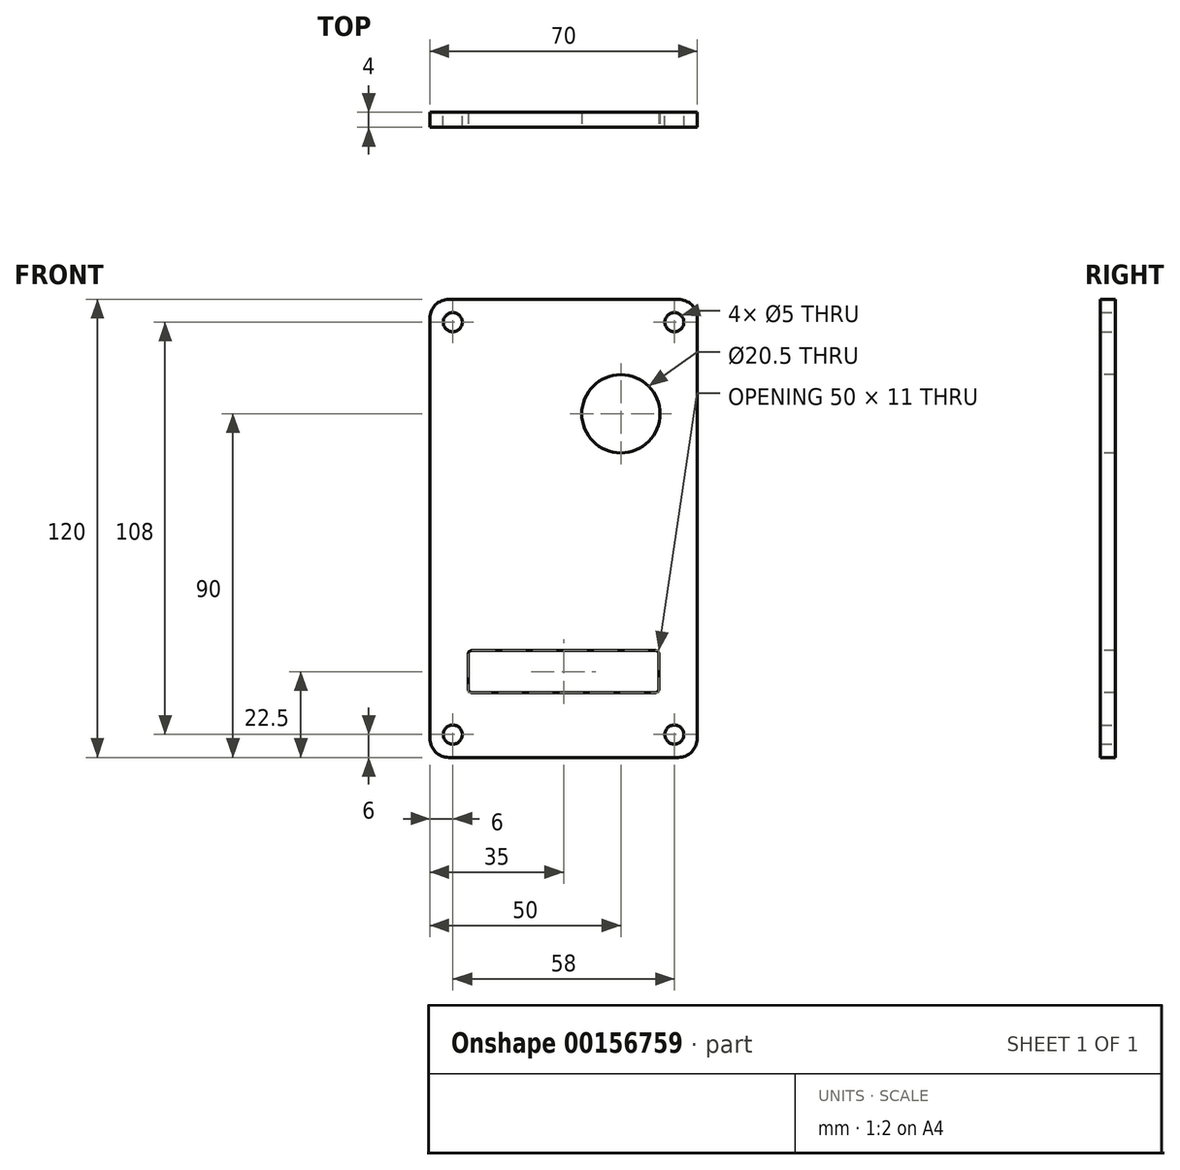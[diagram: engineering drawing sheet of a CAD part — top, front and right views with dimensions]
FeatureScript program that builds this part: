
annotation { "Feature Type Name" : "Feature", "Feature Type Description" : "" }
export const myFeature = defineFeature(function(context is Context, id is Id, definition is map)
    precondition{}
    {
        {
            var Q0;
            Q0=qCreatedBy(makeId("Front.planeOp"),FACE);
            var sketch = newSketch(context, id + "F0", { "sketchPlane" : qUnion([Q0])});
            skLineSegment(sketch, "E0.bottom", {"start": v(-35, 60) * mm, "end": v(35, 60) * mm});
            skLineSegment(sketch, "E0.top", {"start": v(-35, -60) * mm, "end": v(35, -60) * mm});
            skLineSegment(sketch, "E0.left", {"start": v(-35, 60) * mm, "end": v(-35, -60) * mm});
            skLineSegment(sketch, "E0.right", {"start": v(35, 60) * mm, "end": v(35, -60) * mm});
            skPoint(sketch, "E0.middle", {"position": v(0, 0) * mm});
            skLineSegment(sketch, "E1.bottom", {"start": v(-29, 54) * mm, "end": v(29, 54) * mm});
            skLineSegment(sketch, "E1.top", {"start": v(-29, -54) * mm, "end": v(29, -54) * mm});
            skLineSegment(sketch, "E1.left", {"start": v(-29, 54) * mm, "end": v(-29, -54) * mm});
            skLineSegment(sketch, "E1.right", {"start": v(29, 54) * mm, "end": v(29, -54) * mm});
            skCircle(sketch, "E2", {"center": v(-29, 54) * mm, "radius": 2.5 * mm});
            skCircle(sketch, "E3.MirrorC", {"center": v(29, 54) * mm, "radius": 2.5 * mm});
            skCircle(sketch, "E4.MirrorC", {"center": v(-29, -54) * mm, "radius": 2.5 * mm});
            skCircle(sketch, "E5.MirrorC", {"center": v(29, -54) * mm, "radius": 2.5 * mm});
            skSolve(sketch);
        }
        {
            var Q0;
            Q0=makeQuery(id+"F0.imprint","IMPRINT",FACE,{"disambiguationData":[TD([[makeQuery(id+"F0.imprint","IMPRINT",EDGE,{"derivedFrom":sQuery(id+"F0.wireOp",EDGE,"E0.bottom")}),-1.0]])]});
            var Q1;
            {var subQ5=sQuery(id+"F0.wireOp",EDGE,"E2");var subQ13=sQuery(id+"F0.wireOp",EDGE,"E1.bottom");var subQ14=makeQuery(id+"F0.imprint","INTERSECT",VERTEX,{"derivedFrom":[subQ13,subQ5]});Q1=makeQuery(id+"F0.imprint","IMPRINT",FACE,{"disambiguationData":[TD([[makeQuery(id+"F0.imprint","IMPRINT",EDGE,{"disambiguationData":[TD([[subQ14,-1.0]])],"derivedFrom":subQ13}),-1.0]])]});}
            extrude(context, id + "F1", {"entities" : qUnion([Q0, Q1]), "depth" : 4 * mm});
        }
        {
            var Q0;
            Q0=makeQuery(id+"F1.opExtrude","SWEPT_EDGE",EDGE,{"disambiguationData":[OSD([sQuery(id+"F0.wireOp",EDGE,"E0.bottom"),sQuery(id+"F0.wireOp",EDGE,"E0.left")])]});
            var Q1;
            Q1=makeQuery(id+"F1.opExtrude","SWEPT_EDGE",EDGE,{"disambiguationData":[OSD([sQuery(id+"F0.wireOp",EDGE,"E0.bottom"),sQuery(id+"F0.wireOp",EDGE,"E0.right")])]});
            var Q2;
            Q2=makeQuery(id+"F1.opExtrude","SWEPT_EDGE",EDGE,{"disambiguationData":[OSD([sQuery(id+"F0.wireOp",EDGE,"E0.top"),sQuery(id+"F0.wireOp",EDGE,"E0.left")])]});
            var Q3;
            Q3=makeQuery(id+"F1.opExtrude","SWEPT_EDGE",EDGE,{"disambiguationData":[OSD([sQuery(id+"F0.wireOp",EDGE,"E0.top"),sQuery(id+"F0.wireOp",EDGE,"E0.right")])]});
            fillet(context, id + "F2", {"entities" : qUnion([Q0, Q1, Q2, Q3]), "radius" : 5 * mm, "tangentPropagation" : true, "allowEdgeOverflow" : false});
        }
        {
            var Q0;
            Q0=makeQuery(id+"F1.opExtrude","CAP_FACE",FACE,{"disambiguationData":[OSD([sQuery(id+"F0.wireOp",EDGE,"E0.bottom"),sQuery(id+"F0.wireOp",EDGE,"E0.top"),sQuery(id+"F0.wireOp",EDGE,"E0.left"),sQuery(id+"F0.wireOp",EDGE,"E0.right"),sQuery(id+"F0.wireOp",EDGE,"E2"),sQuery(id+"F0.wireOp",EDGE,"E3.MirrorC"),sQuery(id+"F0.wireOp",EDGE,"E4.MirrorC"),sQuery(id+"F0.wireOp",EDGE,"E5.MirrorC")])],"isStart":false});
            var sketch = newSketch(context, id + "F3", { "sketchPlane" : qUnion([Q0])});
            skPoint(sketch, "E6", {"position": v(15, 30) * mm});
            skCircle(sketch, "E7", {"center": v(15, 30) * mm, "radius": 10.25 * mm});
            skSolve(sketch);
        }
        {
            var Q0;
            Q0 = qSketchRegion(id + "F3", true);
            extrude(context, id + "F4", {"entities" : qUnion([Q0]), "operationType" : NewBodyOperationType.REMOVE, "oppositeDirection" : true, "depth" : 25 * mm});
        }
        {
            var Q0;
            Q0=makeQuery(id+"F1.opExtrude","CAP_FACE",FACE,{"disambiguationData":[OSD([sQuery(id+"F0.wireOp",EDGE,"E0.bottom"),sQuery(id+"F0.wireOp",EDGE,"E0.top"),sQuery(id+"F0.wireOp",EDGE,"E0.left"),sQuery(id+"F0.wireOp",EDGE,"E0.right"),sQuery(id+"F0.wireOp",EDGE,"E2"),sQuery(id+"F0.wireOp",EDGE,"E3.MirrorC"),sQuery(id+"F0.wireOp",EDGE,"E4.MirrorC"),sQuery(id+"F0.wireOp",EDGE,"E5.MirrorC")])],"isStart":false});
            var sketch = newSketch(context, id + "F5", { "sketchPlane" : qUnion([Q0])});
            skLineSegment(sketch, "E8.bottom", {"start": v(-25, -32) * mm, "end": v(25, -32) * mm});
            skLineSegment(sketch, "E8.top", {"start": v(-25, -43) * mm, "end": v(25, -43) * mm});
            skLineSegment(sketch, "E8.left", {"start": v(-25, -32) * mm, "end": v(-25, -43) * mm});
            skLineSegment(sketch, "E8.right", {"start": v(25, -32) * mm, "end": v(25, -43) * mm});
            skSolve(sketch);
        }
        {
            var Q0;
            Q0 = qSketchRegion(id + "F5", true);
            extrude(context, id + "F6", {"entities" : qUnion([Q0]), "operationType" : NewBodyOperationType.REMOVE, "oppositeDirection" : true, "depth" : 25 * mm});
        }
        {
            var Q0;
            Q0=makeQuery(id+"F6.boolean.opBoolean","COPY",EDGE,{"derivedFrom":makeQuery(id+"F6.opExtrude","SWEPT_EDGE",EDGE,{"disambiguationData":[OSD([sQuery(id+"F5.wireOp",EDGE,"E8.top"),sQuery(id+"F5.wireOp",EDGE,"E8.left")])]})});
            var Q1;
            Q1=makeQuery(id+"F6.boolean.opBoolean","COPY",EDGE,{"derivedFrom":makeQuery(id+"F6.opExtrude","SWEPT_EDGE",EDGE,{"disambiguationData":[OSD([sQuery(id+"F5.wireOp",EDGE,"E8.bottom"),sQuery(id+"F5.wireOp",EDGE,"E8.left")])]})});
            var Q2;
            Q2=makeQuery(id+"F6.boolean.opBoolean","COPY",EDGE,{"derivedFrom":makeQuery(id+"F6.opExtrude","SWEPT_EDGE",EDGE,{"disambiguationData":[OSD([sQuery(id+"F5.wireOp",EDGE,"E8.bottom"),sQuery(id+"F5.wireOp",EDGE,"E8.right")])]})});
            var Q3;
            Q3=makeQuery(id+"F6.boolean.opBoolean","COPY",EDGE,{"derivedFrom":makeQuery(id+"F6.opExtrude","SWEPT_EDGE",EDGE,{"disambiguationData":[OSD([sQuery(id+"F5.wireOp",EDGE,"E8.top"),sQuery(id+"F5.wireOp",EDGE,"E8.right")])]})});
            fillet(context, id + "F7", {"entities" : qUnion([Q0, Q1, Q2, Q3]), "radius" : 1 * mm, "tangentPropagation" : true, "allowEdgeOverflow" : false});
        }
    });
